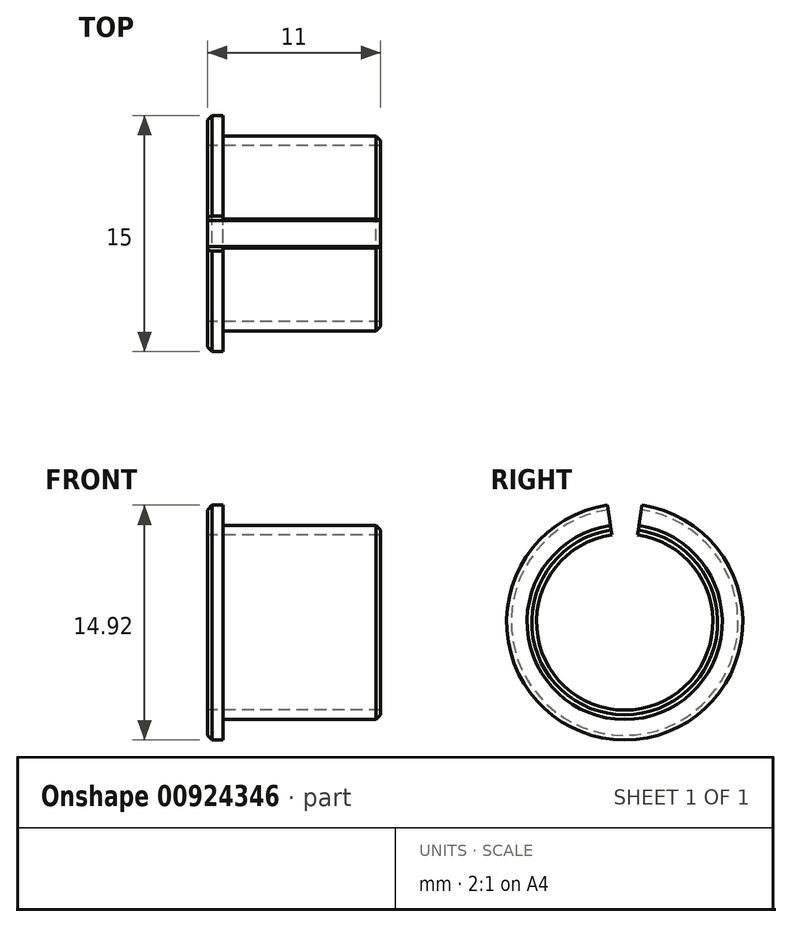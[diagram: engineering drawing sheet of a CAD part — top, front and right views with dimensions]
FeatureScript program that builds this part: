
annotation { "Feature Type Name" : "Feature", "Feature Type Description" : "" }
export const myFeature = defineFeature(function(context is Context, id is Id, definition is map)
    precondition{}
    {
        {
            var Q0;
            Q0=qCreatedBy(makeId("Right.planeOp"),FACE);
            var sketch = newSketch(context, id + "F0", { "sketchPlane" : qUnion([Q0])});
            skCircle(sketch, "E0", {"center": v(0, 0) * mm, "radius": 7.5 * mm});
            skCircle(sketch, "E1", {"center": v(0, 0) * mm, "radius": 6.2 * mm});
            skCircle(sketch, "E2", {"center": v(0, 0) * mm, "radius": 5.6 * mm});
            skSolve(sketch);
        }
        {
            var Q0;
            Q0=makeQuery(id+"F0.imprint","IMPRINT",FACE,{"disambiguationData":[TD([[makeQuery(id+"F0.imprint","IMPRINT",EDGE,{"derivedFrom":sQuery(id+"F0.wireOp",EDGE,"E1")}),1.0]])]});
            var Q1;
            Q1=makeQuery(id+"F0.imprint","IMPRINT",FACE,{"disambiguationData":[TD([[makeQuery(id+"F0.imprint","IMPRINT",EDGE,{"derivedFrom":sQuery(id+"F0.wireOp",EDGE,"E2")}),1.0]])]});
            var Q2;
            Q2=makeQuery(id+"F0.imprint","IMPRINT",FACE,{"disambiguationData":[TD([[makeQuery(id+"F0.imprint","IMPRINT",EDGE,{"derivedFrom":sQuery(id+"F0.wireOp",EDGE,"E0")}),1.0]])]});
            extrude(context, id + "F1", {"entities" : qUnion([Q0, Q1, Q2]), "depth" : 1 * mm, "offsetDistance" : 25 * mm});
        }
        {
            var Q0;
            Q0=makeQuery(id+"F0.imprint","IMPRINT",FACE,{"disambiguationData":[TD([[makeQuery(id+"F0.imprint","IMPRINT",EDGE,{"derivedFrom":sQuery(id+"F0.wireOp",EDGE,"E1")}),1.0]])]});
            extrude(context, id + "F2", {"entities" : qUnion([Q0]), "operationType" : NewBodyOperationType.ADD, "depth" : 11 * mm, "offsetDistance" : 25 * mm});
        }
        {
            var Q0;
            Q0=makeQuery(id+"F0.imprint","IMPRINT",FACE,{"disambiguationData":[TD([[makeQuery(id+"F0.imprint","IMPRINT",EDGE,{"derivedFrom":sQuery(id+"F0.wireOp",EDGE,"E2")}),1.0]])]});
            extrude(context, id + "F3", {"entities" : qUnion([Q0]), "operationType" : NewBodyOperationType.REMOVE, "endBound" : BoundingType.THROUGH_ALL, "depth" : 25 * mm, "offsetDistance" : 25 * mm});
        }
        {
            var Q0;
            Q0=makeQuery(id+"F3.boolean.opBoolean","COPY",EDGE,{"derivedFrom":makeQuery(id+"F3.opExtrude","CAP_EDGE",EDGE,{"disambiguationData":[OSD([sQuery(id+"F0.wireOp",EDGE,"E2")])],"isStart":true})});
            var Q1;
            Q1=makeQuery(id+"F2.opExtrude","CAP_EDGE",EDGE,{"disambiguationData":[OSD([sQuery(id+"F0.wireOp",EDGE,"E1")])],"isStart":false});
            var Q2;
            Q2=makeQuery(id+"F1.opExtrude","CAP_EDGE",EDGE,{"disambiguationData":[OSD([sQuery(id+"F0.wireOp",EDGE,"E0")])],"isStart":true});
            chamfer(context, id + "F4", {"entities" : qUnion([Q0, Q1, Q2]), "width" : 0.3 * mm, "tangentPropagation" : true});
        }
        {
            var Q0;
            Q0=qCreatedBy(makeId("Right.planeOp"),FACE);
            var sketch = newSketch(context, id + "F5", { "sketchPlane" : qUnion([Q0])});
            skArc(sketch, "E3.0", {"start": v(-7.5, 0) * mm, "mid": v(0, -7.5) * mm, "end": v(7.5, 0) * mm, "construction": true});
            skLineSegment(sketch, "E4", {"start": v(0, 9.89) * mm, "end": v(0, -10.3) * mm, "construction": true});
            skLineSegment(sketch, "E5", {"start": v(10.94, 0) * mm, "end": v(-10.87, 0) * mm, "construction": true});
            skCircle(sketch, "E6.0", {"center": v(0, 0) * mm, "radius": 5.6 * mm, "construction": true});
            skLineSegment(sketch, "E7", {"start": v(0, 0) * mm, "end": v(1.25, 8.4) * mm, "construction": true});
            skLineSegment(sketch, "E8", {"start": v(0, 0) * mm, "end": v(-1.25, 8.4) * mm, "construction": true});
            skLineSegment(sketch, "E9", {"start": v(1.25, 8.4) * mm, "end": v(-1.25, 8.4) * mm, "construction": true});
            skArc(sketch, "E10.trimOffspring", {"start": v(1.1, 7.42) * mm, "mid": v(0, 7.5) * mm, "end": v(-1.1, 7.42) * mm, "construction": true});
            skArc(sketch, "E11.trimOffspring", {"start": v(1.25, 8.4) * mm, "mid": v(0, 8.5) * mm, "end": v(-1.25, 8.4) * mm});
            skArc(sketch, "E12.trimOffspring", {"start": v(0.59, 3.96) * mm, "mid": v(0, 4) * mm, "end": v(-0.59, 3.96) * mm});
            skLineSegment(sketch, "E13", {"start": v(1.25, 8.4) * mm, "end": v(0.59, 3.96) * mm});
            skLineSegment(sketch, "E14", {"start": v(-1.25, 8.4) * mm, "end": v(-0.59, 3.96) * mm});
            skSolve(sketch);
        }
        {
            var Q0;
            Q0=makeQuery(id+"F5.imprint","IMPRINT",FACE,{"disambiguationData":[TD([[makeQuery(id+"F5.imprint","IMPRINT",EDGE,{"derivedFrom":sQuery(id+"F5.wireOp",EDGE,"E11.trimOffspring")}),1.0]])]});
            extrude(context, id + "F6", {"entities" : qUnion([Q0]), "operationType" : NewBodyOperationType.REMOVE, "endBound" : BoundingType.THROUGH_ALL, "depth" : 25 * mm, "offsetDistance" : 25 * mm});
        }
    });
